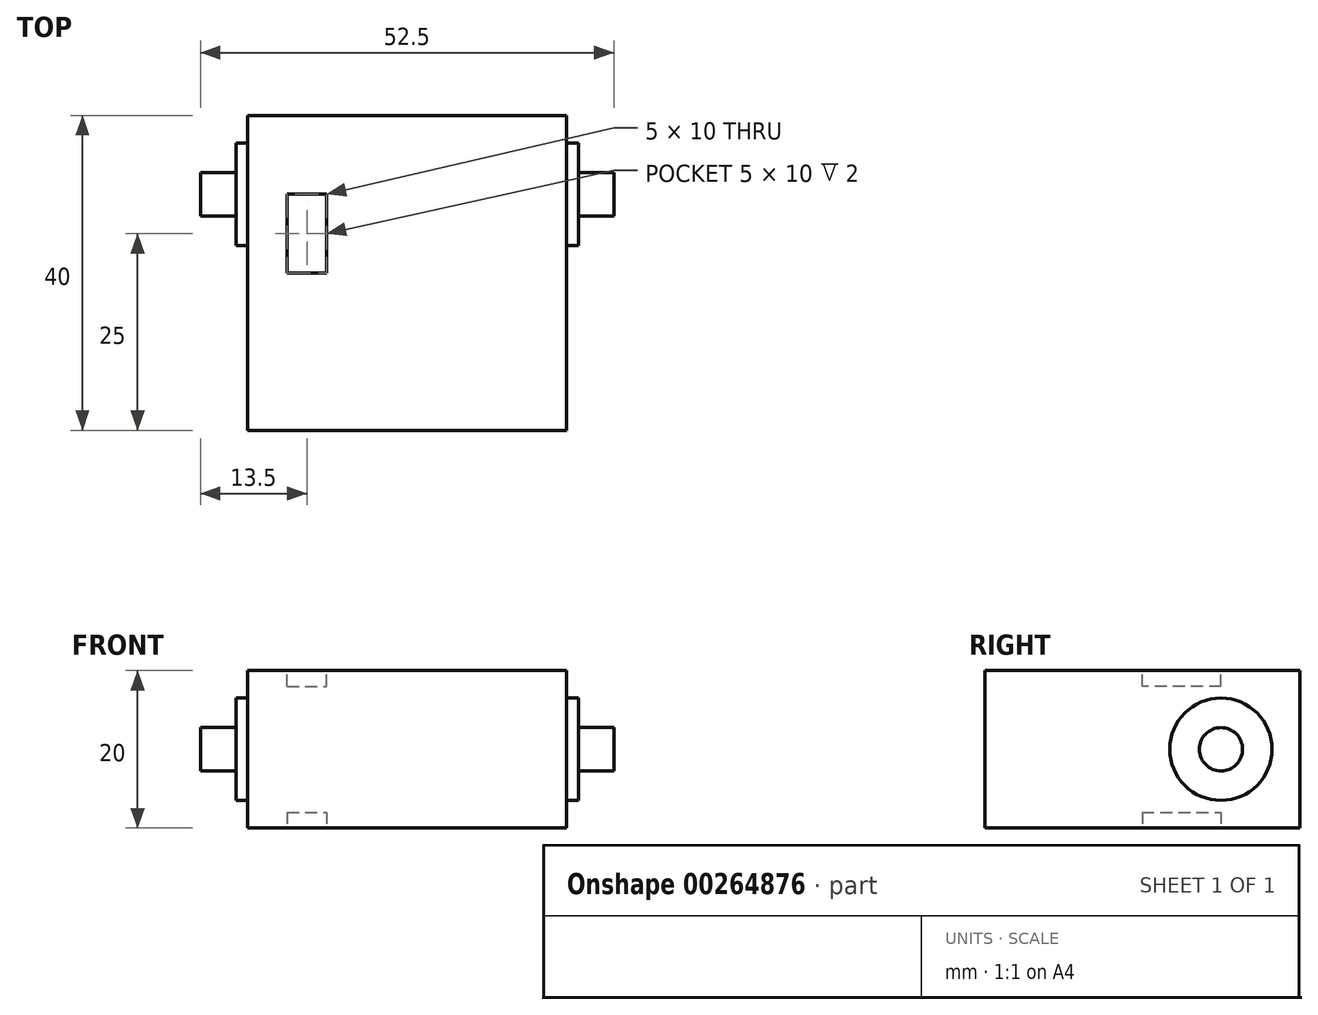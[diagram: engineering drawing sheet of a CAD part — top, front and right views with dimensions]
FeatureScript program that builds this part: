
annotation { "Feature Type Name" : "Feature", "Feature Type Description" : "" }
export const myFeature = defineFeature(function(context is Context, id is Id, definition is map)
    precondition{}
    {
        {
            var Q0;
            Q0=qCreatedBy(makeId("Top.planeOp"),FACE);
            var sketch = newSketch(context, id + "F0", { "sketchPlane" : qUnion([Q0])});
            skLineSegment(sketch, "E0.bottom", {"start": v(-20.25, 20) * mm, "end": v(20.25, 20) * mm});
            skLineSegment(sketch, "E0.top", {"start": v(-20.25, -20) * mm, "end": v(20.25, -20) * mm});
            skLineSegment(sketch, "E0.left", {"start": v(-20.25, 20) * mm, "end": v(-20.25, -20) * mm});
            skLineSegment(sketch, "E0.right", {"start": v(20.25, 20) * mm, "end": v(20.25, -20) * mm});
            skSolve(sketch);
        }
        {
            var Q0;
            Q0=makeQuery(id+"F0.imprint","IMPRINT",FACE,{"disambiguationData":[TD([[makeQuery(id+"F0.imprint","IMPRINT",EDGE,{"derivedFrom":sQuery(id+"F0.wireOp",EDGE,"E0.bottom")}),-1.0]])]});
            extrude(context, id + "F1", {"entities" : qUnion([Q0]), "oppositeDirection" : true, "depth" : 20 * mm, "symmetric" : true});
        }
        {
            var Q0;
            Q0=makeQuery(id+"F1.opExtrude","SWEPT_FACE",FACE,{"disambiguationData":[OSD([sQuery(id+"F0.wireOp",EDGE,"E0.left")])]});
            var sketch = newSketch(context, id + "F2", { "sketchPlane" : qUnion([Q0])});
            skLineSegment(sketch, "E1.bottom", {"start": v(-20, 10) * mm, "end": v(-10, 10) * mm});
            skLineSegment(sketch, "E1.top", {"start": v(-20, -10) * mm, "end": v(-10, -10) * mm});
            skLineSegment(sketch, "E1.left", {"start": v(-20, 10) * mm, "end": v(-20, -10) * mm});
            skLineSegment(sketch, "E1.right", {"start": v(-10, 10) * mm, "end": v(-10, -10) * mm});
            skPoint(sketch, "E2", {"position": v(-10, 0) * mm});
            skCircle(sketch, "E3", {"center": v(-10, 0) * mm, "radius": 6.5 * mm});
            skSolve(sketch);
        }
        {
            var Q0;
            {var subQ0=sQuery(id+"F2.wireOp",EDGE,"E3");var subQ1=sQuery(id+"F2.wireOp",EDGE,"E1.right");var subQ2=makeQuery(id+"F2.imprint","INTERSECT",VERTEX,{"disambiguationData":[OD(0.0)],"derivedFrom":[subQ1,subQ0]});Q0=makeQuery(id+"F2.imprint","IMPRINT",FACE,{"disambiguationData":[TD([[makeQuery(id+"F2.imprint","IMPRINT",EDGE,{"disambiguationData":[TD([[subQ2,-1.0]])],"derivedFrom":subQ1}),-1.0]])]});}
            var Q1;
            {var subQ0=sQuery(id+"F2.wireOp",EDGE,"E3");var subQ1=sQuery(id+"F2.wireOp",EDGE,"E1.right");var subQ2=makeQuery(id+"F2.imprint","INTERSECT",VERTEX,{"disambiguationData":[OD(0.0)],"derivedFrom":[subQ1,subQ0]});Q1=makeQuery(id+"F2.imprint","IMPRINT",FACE,{"disambiguationData":[TD([[makeQuery(id+"F2.imprint","IMPRINT",EDGE,{"disambiguationData":[TD([[subQ2,-1.0]])],"derivedFrom":subQ1}),1.0]])]});}
            extrude(context, id + "F3", {"entities" : qUnion([Q0, Q1]), "operationType" : NewBodyOperationType.ADD, "depth" : 1.5 * mm});
        }
        {
            var Q0;
            Q0=makeQuery(id+"F3.opExtrude","CAP_FACE",FACE,{"disambiguationData":[OSD([sQuery(id+"F2.wireOp",EDGE,"E3")])],"isStart":false});
            var sketch = newSketch(context, id + "F4", { "sketchPlane" : qUnion([Q0])});
            skCircle(sketch, "E4", {"center": v(-10, 0) * mm, "radius": 2.75 * mm});
            skSolve(sketch);
        }
        {
            var Q0;
            Q0=makeQuery(id+"F4.imprint","IMPRINT",FACE,{"disambiguationData":[TD([[makeQuery(id+"F4.imprint","IMPRINT",EDGE,{"derivedFrom":sQuery(id+"F4.wireOp",EDGE,"E4")}),1.0]])]});
            extrude(context, id + "F5", {"entities" : qUnion([Q0]), "operationType" : NewBodyOperationType.ADD, "depth" : 4.5 * mm});
        }
        {
            var Q0;
            Q0=makeQuery(id+"F1.opExtrude","SWEPT_FACE",FACE,{"disambiguationData":[OSD([sQuery(id+"F0.wireOp",EDGE,"E0.right")])]});
            var sketch = newSketch(context, id + "F6", { "sketchPlane" : qUnion([Q0])});
            skLineSegment(sketch, "E5.bottom", {"start": v(20, 10) * mm, "end": v(10, 10) * mm});
            skLineSegment(sketch, "E5.top", {"start": v(20, -10) * mm, "end": v(10, -10) * mm});
            skLineSegment(sketch, "E5.left", {"start": v(20, 10) * mm, "end": v(20, -10) * mm});
            skLineSegment(sketch, "E5.right", {"start": v(10, 10) * mm, "end": v(10, -10) * mm});
            skCircle(sketch, "E6", {"center": v(10, 0) * mm, "radius": 6.5 * mm});
            skSolve(sketch);
        }
        {
            var Q0;
            {var subQ0=sQuery(id+"F6.wireOp",EDGE,"E6");var subQ1=sQuery(id+"F6.wireOp",EDGE,"E5.right");var subQ2=makeQuery(id+"F6.imprint","INTERSECT",VERTEX,{"disambiguationData":[OD(0.0)],"derivedFrom":[subQ1,subQ0]});Q0=makeQuery(id+"F6.imprint","IMPRINT",FACE,{"disambiguationData":[TD([[makeQuery(id+"F6.imprint","IMPRINT",EDGE,{"disambiguationData":[TD([[subQ2,-1.0]])],"derivedFrom":subQ1}),1.0]])]});}
            var Q1;
            {var subQ0=sQuery(id+"F6.wireOp",EDGE,"E6");var subQ1=sQuery(id+"F6.wireOp",EDGE,"E5.right");var subQ2=makeQuery(id+"F6.imprint","INTERSECT",VERTEX,{"disambiguationData":[OD(0.0)],"derivedFrom":[subQ1,subQ0]});Q1=makeQuery(id+"F6.imprint","IMPRINT",FACE,{"disambiguationData":[TD([[makeQuery(id+"F6.imprint","IMPRINT",EDGE,{"disambiguationData":[TD([[subQ2,-1.0]])],"derivedFrom":subQ1}),-1.0]])]});}
            extrude(context, id + "F7", {"entities" : qUnion([Q0, Q1]), "operationType" : NewBodyOperationType.ADD, "depth" : 1.5 * mm});
        }
        {
            var Q0;
            Q0=makeQuery(id+"F7.opExtrude","CAP_FACE",FACE,{"disambiguationData":[OSD([sQuery(id+"F6.wireOp",EDGE,"E6")])],"isStart":false});
            var sketch = newSketch(context, id + "F8", { "sketchPlane" : qUnion([Q0])});
            skCircle(sketch, "E7", {"center": v(10, 0) * mm, "radius": 2.75 * mm});
            skSolve(sketch);
        }
        {
            var Q0;
            Q0=makeQuery(id+"F8.imprint","IMPRINT",FACE,{"disambiguationData":[TD([[makeQuery(id+"F8.imprint","IMPRINT",EDGE,{"derivedFrom":sQuery(id+"F8.wireOp",EDGE,"E7")}),1.0]])]});
            extrude(context, id + "F9", {"entities" : qUnion([Q0]), "operationType" : NewBodyOperationType.ADD, "depth" : 4.5 * mm});
        }
        {
            var Q0;
            Q0=makeQuery(id+"F1.opExtrude","CAP_FACE",FACE,{"disambiguationData":[OSD([sQuery(id+"F0.wireOp",EDGE,"E0.bottom"),sQuery(id+"F0.wireOp",EDGE,"E0.top"),sQuery(id+"F0.wireOp",EDGE,"E0.left"),sQuery(id+"F0.wireOp",EDGE,"E0.right")])],"isStart":false});
            var sketch = newSketch(context, id + "F10", { "sketchPlane" : qUnion([Q0])});
            skLineSegment(sketch, "E8.bottom", {"start": v(-15.25, 0) * mm, "end": v(-10.25, 0) * mm});
            skLineSegment(sketch, "E8.top", {"start": v(-15.25, -10) * mm, "end": v(-10.25, -10) * mm});
            skLineSegment(sketch, "E8.left", {"start": v(-15.25, 0) * mm, "end": v(-15.25, -10) * mm});
            skLineSegment(sketch, "E8.right", {"start": v(-10.25, 0) * mm, "end": v(-10.25, -10) * mm});
            skSolve(sketch);
        }
        {
            var Q0;
            Q0=makeQuery(id+"F10.imprint","IMPRINT",FACE,{"disambiguationData":[TD([[makeQuery(id+"F10.imprint","IMPRINT",EDGE,{"derivedFrom":sQuery(id+"F10.wireOp",EDGE,"E8.bottom")}),-1.0]])]});
            extrude(context, id + "F11", {"entities" : qUnion([Q0]), "operationType" : NewBodyOperationType.REMOVE, "oppositeDirection" : true, "depth" : 2 * mm});
        }
        {
            var Q0;
            Q0=makeQuery(id+"F1.opExtrude","CAP_FACE",FACE,{"disambiguationData":[OSD([sQuery(id+"F0.wireOp",EDGE,"E0.bottom"),sQuery(id+"F0.wireOp",EDGE,"E0.top"),sQuery(id+"F0.wireOp",EDGE,"E0.left"),sQuery(id+"F0.wireOp",EDGE,"E0.right")])],"isStart":true});
            var sketch = newSketch(context, id + "F12", { "sketchPlane" : qUnion([Q0])});
            skLineSegment(sketch, "E9.bottom", {"start": v(-15.25, 10) * mm, "end": v(-10.25, 10) * mm});
            skLineSegment(sketch, "E9.top", {"start": v(-15.25, 0) * mm, "end": v(-10.25, 0) * mm});
            skLineSegment(sketch, "E9.left", {"start": v(-15.25, 10) * mm, "end": v(-15.25, 0) * mm});
            skLineSegment(sketch, "E9.right", {"start": v(-10.25, 10) * mm, "end": v(-10.25, 0) * mm});
            skSolve(sketch);
        }
        {
            var Q0;
            Q0=makeQuery(id+"F12.imprint","IMPRINT",FACE,{"disambiguationData":[TD([[makeQuery(id+"F12.imprint","IMPRINT",EDGE,{"derivedFrom":sQuery(id+"F12.wireOp",EDGE,"E9.bottom")}),-1.0]])]});
            extrude(context, id + "F13", {"entities" : qUnion([Q0]), "operationType" : NewBodyOperationType.REMOVE, "oppositeDirection" : true, "depth" : 2 * mm});
        }
    });
